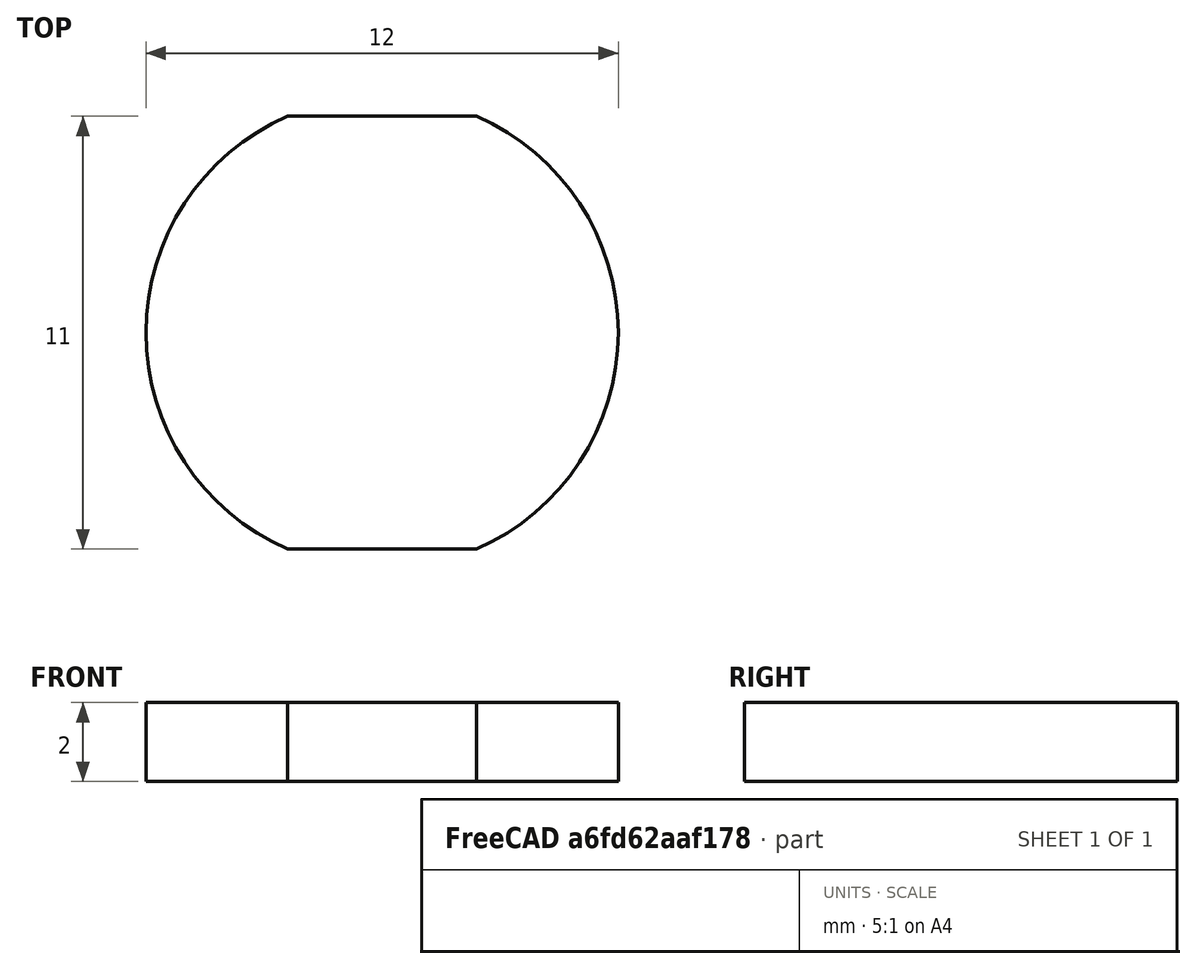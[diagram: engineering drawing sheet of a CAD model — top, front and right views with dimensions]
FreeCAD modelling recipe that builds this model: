
FCSTD DOCUMENT  (FreeCAD 0.18.4R)
Label: button_hole
License: All rights reserved
LicenseURL: http://en.wikipedia.org/wiki/All_rights_reserved
objects: Sketcher::SketchObject×1, PartDesign::Pad×1, PartDesign::Body×1, TechDraw::DrawSVGTemplate×1, TechDraw::DrawViewPart×1, TechDraw::DrawPage×1
note: 4 computed .brp shape members not serialized (recipe doc carries the construction recipe); baked Part::Feature solids carry a one-line shape summary decoded from their .brp

FEATURE [Sketcher::SketchObject] Sketch
  expr: Constraints[4] = 12 / 2
  sketch-geometry (4):
    g0: LineSegment StartX=-2.39792 StartY=5.5 StartZ=0 EndX=2.39792 EndY=5.5 EndZ=0
    g1: ArcOfCircle CenterX=0 CenterY=0 CenterZ=0 NormalX=0 NormalY=0 NormalZ=1 AngleXU=0 Radius=6 StartAngle=1.98193 EndAngle=4.30125
    g2: LineSegment StartX=-2.39792 StartY=-5.5 StartZ=0 EndX=2.39792 EndY=-5.5 EndZ=0
    g3: ArcOfCircle CenterX=0 CenterY=0 CenterZ=0 NormalX=0 NormalY=0 NormalZ=1 AngleXU=0 Radius=6 StartAngle=5.12353 EndAngle=7.44284
  constraints (11):
    c: Horizontal(g0)
    c: Coincident(g1,g-1)
    c: Coincident(g3,g0)
    c: Coincident(g1,g0)
    c: Radius(g1) = 6
    c: Horizontal(g2)
    c: Coincident(g1,g2)
    c: Coincident(g3,g2)
    c: Coincident(g1,g3)
    c: Symmetric(g1,g0,g1)
    c: DistanceY(g1,g0) = 11
FEATURE [PartDesign::Pad] Pad
  Length = 2
  Length2 = 100
  Profile = -> Sketch
  Refine = true
  Type = 0
FEATURE [PartDesign::Body] Body
  Group = -> [Sketch,Pad]
  Origin = -> Origin
  Tip = -> Pad
FEATURE [TechDraw::DrawSVGTemplate] Template
  Height = 210
  Orientation = 1
  Width = 297
FEATURE [TechDraw::DrawViewPart] View
  CoarseView = false
  Direction = (0,0,1)
  Focus = 100
  HardHidden = false
  IsoCount = 0
  IsoHidden = false
  IsoVisible = false
  LockPosition = false
  Perspective = false
  Rotation = 0
  ScaleType = 0
  SeamHidden = false
  SeamVisible = false
  SmoothHidden = false
  SmoothVisible = false
  Source = -> [Body]
  X = 148.5
  Y = 105
FEATURE [TechDraw::DrawPage] Page
  KeepUpdated = true
  ProjectionType = 0
  Template = -> Template
  Views = -> [View]
